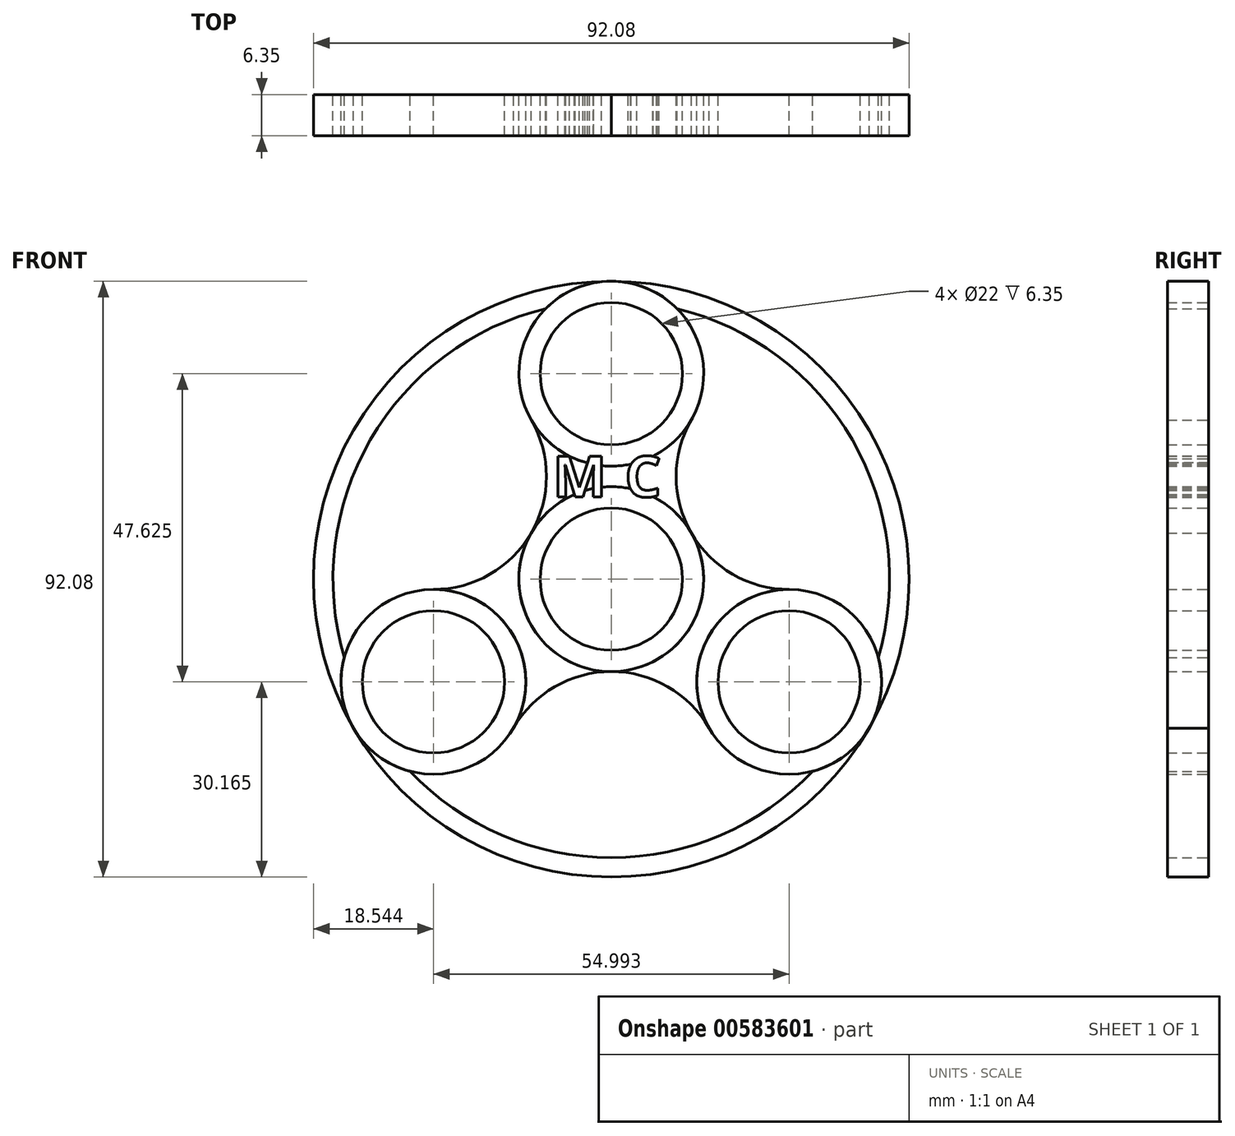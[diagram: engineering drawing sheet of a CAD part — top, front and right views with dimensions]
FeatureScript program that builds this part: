
annotation { "Feature Type Name" : "Feature", "Feature Type Description" : "" }
export const myFeature = defineFeature(function(context is Context, id is Id, definition is map)
    precondition{}
    {
        {
            var Q0;
            Q0=qCreatedBy(makeId("Front.planeOp"),FACE);
            var sketch = newSketch(context, id + "F0", { "sketchPlane" : qUnion([Q0])});
            skCircle(sketch, "E0", {"center": v(0, 0) * mm, "radius": 14.29 * mm});
            skCircle(sketch, "E1", {"center": v(0, 0) * mm, "radius": 11 * mm});
            skCircle(sketch, "E2", {"center": v(0, 31.75) * mm, "radius": 14.29 * mm});
            skCircle(sketch, "E3", {"center": v(0, 31.75) * mm, "radius": 11 * mm});
            skCircle(sketch, "E4.1.0", {"center": v(-27.5, -15.87) * mm, "radius": 11 * mm});
            skCircle(sketch, "E4.1.1", {"center": v(-27.5, -15.87) * mm, "radius": 14.29 * mm});
            skCircle(sketch, "E4.2.0", {"center": v(27.5, -15.88) * mm, "radius": 11 * mm});
            skCircle(sketch, "E4.2.1", {"center": v(27.5, -15.88) * mm, "radius": 14.29 * mm});
            skSolve(sketch);
        }
        {
            var Q0;
            Q0=qCreatedBy(makeId("Front.planeOp"),FACE);
            var sketch = newSketch(context, id + "F1", { "sketchPlane" : qUnion([Q0])});
            skCircle(sketch, "E5.0", {"center": v(0, 31.75) * mm, "radius": 14.29 * mm});
            skCircle(sketch, "E6.0", {"center": v(-27.5, -15.87) * mm, "radius": 14.29 * mm});
            skCircle(sketch, "E6.1", {"center": v(0, 0) * mm, "radius": 14.29 * mm});
            skCircle(sketch, "E6.2", {"center": v(27.5, -15.88) * mm, "radius": 14.29 * mm});
            skArc(sketch, "E7", {"start": v(-27.5, -1.59) * mm, "mid": v(-12.37, 7.14) * mm, "end": v(-12.37, 24.6) * mm});
            skArc(sketch, "E8", {"start": v(12.37, 24.6) * mm, "mid": v(12.37, 7.14) * mm, "end": v(27.5, -1.59) * mm});
            skArc(sketch, "E9", {"start": v(15.12, -23.02) * mm, "mid": v(0, -14.29) * mm, "end": v(-15.12, -23.02) * mm});
            skCircle(sketch, "E10", {"center": v(0, 0) * mm, "radius": 46.04 * mm});
            skCircle(sketch, "E11", {"center": v(0, 0) * mm, "radius": 43.02 * mm});
            skSolve(sketch);
        }
        {
            var Q0;
            Q0=makeQuery(id+"F0.imprint","IMPRINT",FACE,{"disambiguationData":[TD([[makeQuery(id+"F0.imprint","IMPRINT",EDGE,{"derivedFrom":sQuery(id+"F0.wireOp",EDGE,"E2")}),1.0]])]});
            var Q1;
            {var subQ0=sQuery(id+"F1.wireOp",EDGE,"E7");var subQ1=sQuery(id+"F1.wireOp",EDGE,"E5.0");var subQ2=makeQuery(id+"F1.imprint","INTERSECT",VERTEX,{"derivedFrom":[subQ1,subQ0]});Q1=makeQuery(id+"F1.imprint","IMPRINT",FACE,{"disambiguationData":[TD([[makeQuery(id+"F1.imprint","IMPRINT",EDGE,{"disambiguationData":[TD([[subQ2,-1.0]])],"derivedFrom":subQ1}),-1.0]])]});}
            var Q2;
            Q2=makeQuery(id+"F0.imprint","IMPRINT",FACE,{"disambiguationData":[TD([[makeQuery(id+"F0.imprint","IMPRINT",EDGE,{"derivedFrom":sQuery(id+"F0.wireOp",EDGE,"E0")}),1.0]])]});
            var Q3;
            {var subQ0=sQuery(id+"F1.wireOp",EDGE,"E7");var subQ1=sQuery(id+"F1.wireOp",EDGE,"E6.0");var subQ2=makeQuery(id+"F1.imprint","INTERSECT",VERTEX,{"derivedFrom":[subQ1,subQ0]});Q3=makeQuery(id+"F1.imprint","IMPRINT",FACE,{"disambiguationData":[TD([[makeQuery(id+"F1.imprint","IMPRINT",EDGE,{"disambiguationData":[TD([[subQ2,1.0]])],"derivedFrom":subQ1}),-1.0]])]});}
            var Q4;
            Q4=makeQuery(id+"F0.imprint","IMPRINT",FACE,{"disambiguationData":[TD([[makeQuery(id+"F0.imprint","IMPRINT",EDGE,{"derivedFrom":sQuery(id+"F0.wireOp",EDGE,"E4.1.0")}),-1.0]])]});
            var Q5;
            {var subQ0=sQuery(id+"F1.wireOp",EDGE,"E8");var subQ1=sQuery(id+"F1.wireOp",EDGE,"E6.1");var subQ2=makeQuery(id+"F1.imprint","INTERSECT",VERTEX,{"derivedFrom":[subQ1,subQ0]});Q5=makeQuery(id+"F1.imprint","IMPRINT",FACE,{"disambiguationData":[TD([[makeQuery(id+"F1.imprint","IMPRINT",EDGE,{"disambiguationData":[TD([[subQ2,1.0]])],"derivedFrom":subQ1}),-1.0]])]});}
            var Q6;
            Q6=makeQuery(id+"F0.imprint","IMPRINT",FACE,{"disambiguationData":[TD([[makeQuery(id+"F0.imprint","IMPRINT",EDGE,{"derivedFrom":sQuery(id+"F0.wireOp",EDGE,"E4.2.0")}),-1.0]])]});
            var Q7;
            {var subQ0=sQuery(id+"F1.wireOp",EDGE,"E10");var subQ1=sQuery(id+"F1.wireOp",EDGE,"E6.0");var subQ2=makeQuery(id+"F1.imprint","INTERSECT",VERTEX,{"derivedFrom":[subQ1,subQ0]});Q7=makeQuery(id+"F1.imprint","IMPRINT",FACE,{"disambiguationData":[TD([[makeQuery(id+"F1.imprint","IMPRINT",EDGE,{"disambiguationData":[TD([[subQ2,-1.0]])],"derivedFrom":subQ1}),-1.0]])]});}
            var Q8;
            {var subQ0=sQuery(id+"F1.wireOp",EDGE,"E10");var subQ1=sQuery(id+"F1.wireOp",EDGE,"E5.0");var subQ2=makeQuery(id+"F1.imprint","INTERSECT",VERTEX,{"derivedFrom":[subQ1,subQ0]});Q8=makeQuery(id+"F1.imprint","IMPRINT",FACE,{"disambiguationData":[TD([[makeQuery(id+"F1.imprint","IMPRINT",EDGE,{"disambiguationData":[TD([[subQ2,-1.0]])],"derivedFrom":subQ1}),-1.0]])]});}
            var Q9;
            {var subQ0=sQuery(id+"F1.wireOp",EDGE,"E10");var subQ1=sQuery(id+"F1.wireOp",EDGE,"E5.0");var subQ2=makeQuery(id+"F1.imprint","INTERSECT",VERTEX,{"derivedFrom":[subQ1,subQ0]});Q9=makeQuery(id+"F1.imprint","IMPRINT",FACE,{"disambiguationData":[TD([[makeQuery(id+"F1.imprint","IMPRINT",EDGE,{"disambiguationData":[TD([[subQ2,1.0]])],"derivedFrom":subQ1}),-1.0]])]});}
            extrude(context, id + "F2", {"entities" : qUnion([Q0, Q1, Q2, Q3, Q4, Q5, Q6, Q7, Q8, Q9]), "depth" : 6.35 * mm, "offsetDistance" : 25.4 * mm});
        }
        {
            var Q0;
            Q0=qCreatedBy(makeId("Front.planeOp"),FACE);
            var sketch = newSketch(context, id + "F3", { "sketchPlane" : qUnion([Q0])});
            skText(sketch, "E12", { "text": "M", "fontName": "OpenSans-Bold.ttf"});
            skText(sketch, "E13", { "text": "C", "fontName": "OpenSans-Bold.ttf"});
            const initialGuessF3  = {"E12": [-0.00906, 0.0127, 1, 0, 0.00635], "E13": [0.00208, 0.0127, 1, 0, 0.00635]};
            skSetInitialGuess(sketch, initialGuessF3);
            skSolve(sketch);
        }
        {
            var Q0;
            Q0 = qSketchRegion(id + "F3", true);
            extrude(context, id + "F4", {"entities" : qUnion([Q0]), "operationType" : NewBodyOperationType.REMOVE, "depth" : 25.4 * mm, "offsetDistance" : 25.4 * mm});
        }
    });
